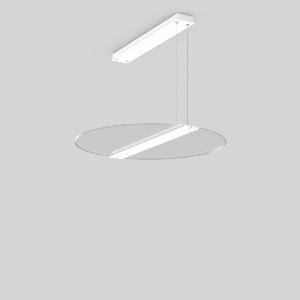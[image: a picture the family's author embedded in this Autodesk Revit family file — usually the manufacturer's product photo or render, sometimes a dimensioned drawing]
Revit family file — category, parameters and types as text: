
# Revit family: twindot_s_round_312353_002_2_76_d5f6
name_source: partatom
category: Lighting Fixtures
units: mm (PartAtom-declared; Revit-internal decimal feet)

## family parameters
Cut with Voids When Loaded = No
Host = Face
Light Source = No
Part Type = Normal
Room Calculation Point = No
Round Connector Dimension = Use Diameter
Shared = No

## types (1)
- TuneableWhite 846 (1 x LED Modul 846, 3100 lm, 4600)
    Apparent Load = 27 VA
    CIE Flux Codes = 47 77 94 56 100
    Color Rendering = 80
    Color Temperature = 4600
    Default Elevation = 1800 mm
    Description = Series: TWINDOT S round
LED pendant luminaire with extremely flat and frameless appearance. Middle bar made of aluminium extrusion profile, powder-coated. Transparent light guide made of UV-resistant acrylic glass (PMMA) with TWINDOT prismatic. Light control with perfectly glare-free TWINDOT technology for pleasantly gentle light with soft shadows. Even and wide indirect and direct light distribution. Direct 55%, indirect 45% light emission. 4-point steel cable suspension, steplessly adjustable. Converter integrated in the canopy (powder-coated white). Power supply through suspension cable. 
Colour: traffic white, matt (RAL 9016)
Diameter: 645 mm
Height: 20 mm
Suspension length: 500-1200 mm
Lamp: LED
Socket: without socket
Colour temperature: 2700K - 6500K
Colour rendering index (CRI): 80
System power: 27 W
Rated luminous flux: 3100 lm
Luminous efficiency: 115 lm/W
System power 2: 28 W
Rated luminous flux 2: 3100 lm
Luminous efficiency 2: 111 lm/W
System power 3: 27 W
Rated luminous flux 3: 3200 lm
Luminous efficiency 3: 119 lm/W
Control gear: Converter, dimmable, DALI
Protection class: I
Type of protection: IP 20
    Height = 20 mm  [stored 0.0656168 ft]
    Lamp = 1 x LED Modul 846
    Lamp Light Flux = 3100 lm
    Lamp count = 1
    Length = 645 mm
    Lifetime = 50000 h
    Luminous efficacy = 115 lm/W
    Manufacturer = RZB
    ModVariant = No
    Model = 312353.002.2.76
    Mounting Place = Ceiling
    Mounting Type = Pendant
    Number of Poles = 1
    OnlyDefault = Yes
    Power Factor = 1
    Product Name = TWINDOT S round
    Product group = Pendant modular luminaires
    ProductGroupID = 906
    Protection Class = Protection class I
    Protection Degree = IP 20
    RLX_Detail_Level = 1
    RLX_Emergency_Light_Flux = 0 lm
    RLX_Emergency_Type = 0
    RLX_Emergency_Type_DB = No
    RlxData = <blob elided: 60505 chars, md5=dafe6ed4>
    Socket = socket
    Standby Power = 0 W
    System Light Flux = 3100 lm
    System Power = 27 W
    Type Comments = TuneableWhite 846
    Type Image = 312353.002.jpg
    URL = http://relux.com
    VarID = tuneablewhite_846
    Voltage = 230 V
    Voltage Range = 220-240 V
    Weight = 0.00 kg
    Width = 0 mm  [stored 0 ft]

note: [stored X ft] marks values corroborated as IEEE doubles in the binary element streams (Revit-internal decimal feet)

## geometry (parser evidence)
native form markers: Blend x4, Sweep x10
no freeform markers — native parametric forms only
